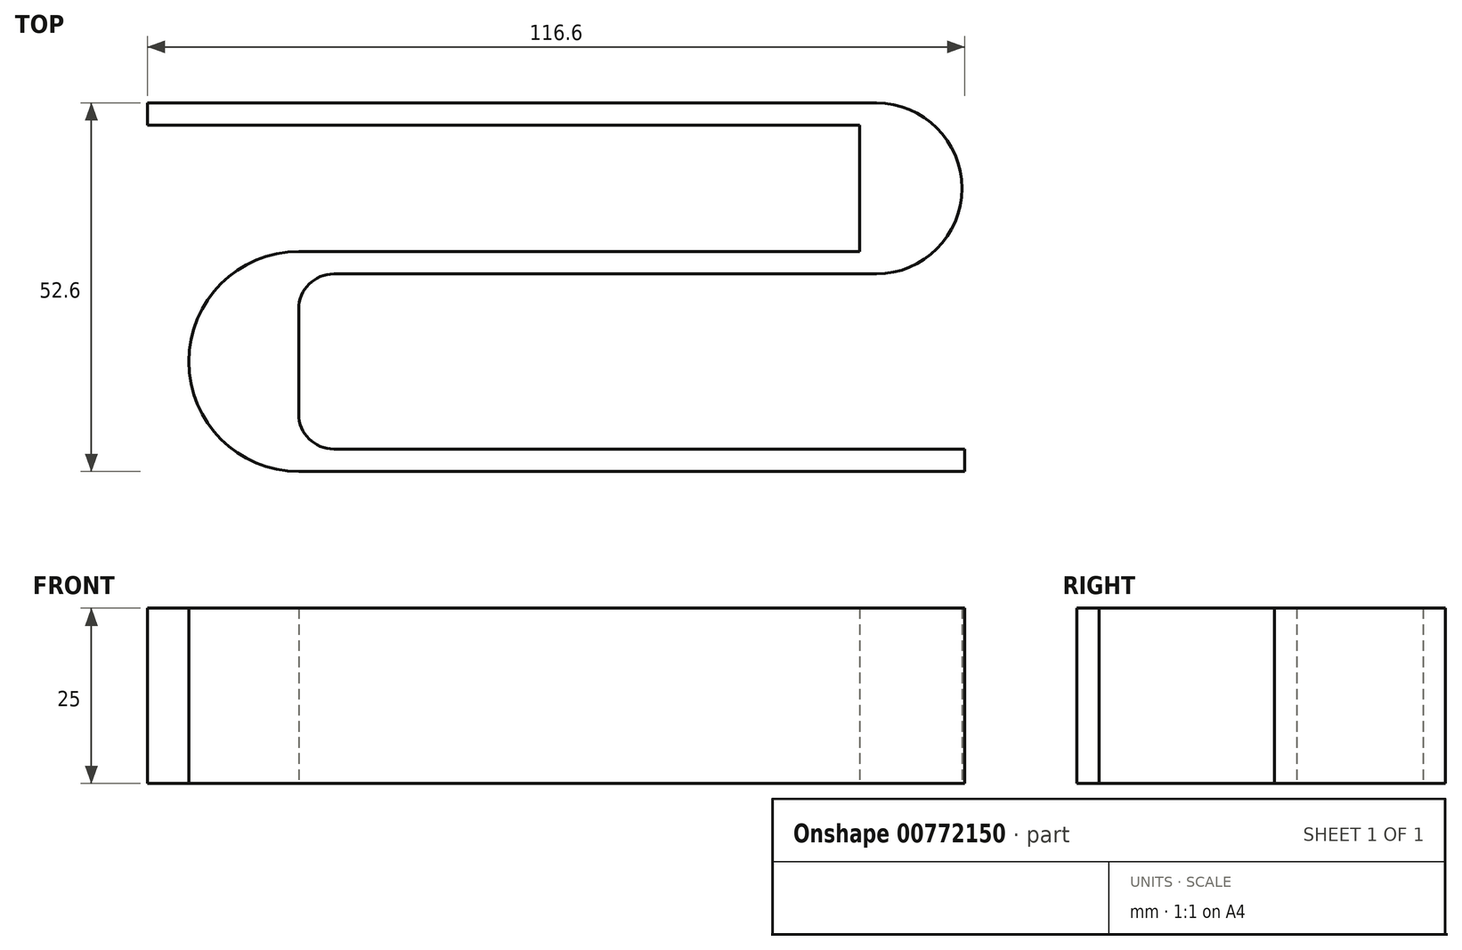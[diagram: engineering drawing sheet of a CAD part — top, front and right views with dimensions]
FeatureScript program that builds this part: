
annotation { "Feature Type Name" : "Feature", "Feature Type Description" : "" }
export const myFeature = defineFeature(function(context is Context, id is Id, definition is map)
    precondition{}
    {
        {
            var Q0;
            Q0=qCreatedBy(makeId("Top.planeOp"),FACE);
            var sketch = newSketch(context, id + "F0", { "sketchPlane" : qUnion([Q0])});
            skLineSegment(sketch, "E0", {"start": v(-21.6, 0) * mm, "end": v(82.4, 0) * mm});
            skLineSegment(sketch, "E1", {"start": v(82.4, 0) * mm, "end": v(82.4, 3.2) * mm});
            skLineSegment(sketch, "E2", {"start": v(82.4, 3.2) * mm, "end": v(-21.6, 3.2) * mm});
            skLineSegment(sketch, "E3", {"start": v(-21.6, 3.2) * mm, "end": v(-21.6, 0) * mm});
            skLineSegment(sketch, "E4", {"start": v(82.4, 0) * mm, "end": v(82.4, -18) * mm});
            skLineSegment(sketch, "E5", {"start": v(82.4, -18) * mm, "end": v(80, -18) * mm});
            skLineSegment(sketch, "E6", {"start": v(80, -18) * mm, "end": v(80, 0) * mm});
            skLineSegment(sketch, "E7", {"start": v(80, -18) * mm, "end": v(0, -18) * mm});
            skLineSegment(sketch, "E8", {"start": v(0, -18) * mm, "end": v(0, -21.2) * mm});
            skLineSegment(sketch, "E9", {"start": v(0, -21.2) * mm, "end": v(82.4, -21.2) * mm});
            skLineSegment(sketch, "E10", {"start": v(82.4, -21.2) * mm, "end": v(82.4, -18) * mm});
            skArc(sketch, "E11", {"start": v(0, -18) * mm, "mid": v(-15.7, -33.7) * mm, "end": v(0, -49.4) * mm});
            skLineSegment(sketch, "E12", {"start": v(0, -21.2) * mm, "end": v(0, -49.4) * mm});
            skArc(sketch, "E13", {"start": v(82.4, -21.2) * mm, "mid": v(94.6, -9) * mm, "end": v(82.4, 3.2) * mm});
            skLineSegment(sketch, "E14", {"start": v(0, -49.4) * mm, "end": v(95, -49.4) * mm});
            skLineSegment(sketch, "E15", {"start": v(0, -46.2) * mm, "end": v(95, -46.2) * mm});
            skLineSegment(sketch, "E16", {"start": v(95, -46.2) * mm, "end": v(95, -49.4) * mm});
            skSolve(sketch);
        }
        {
            var Q0;
            {var subQ0=sQuery(id+"F0.wireOp",EDGE,"E1");Q0=makeQuery(id+"F0.imprint","IMPRINT",FACE,{"disambiguationData":[TD([[makeQuery(id+"F0.imprint","IMPRINT",EDGE,{"derivedFrom":subQ0}),1.0]])]});}
            var Q1;
            {var subQ0=sQuery(id+"F0.wireOp",EDGE,"E4");Q1=makeQuery(id+"F0.imprint","IMPRINT",FACE,{"disambiguationData":[TD([[makeQuery(id+"F0.imprint","IMPRINT",EDGE,{"derivedFrom":subQ0}),-1.0]])]});}
            var Q2;
            Q2=makeQuery(id+"F0.imprint","IMPRINT",FACE,{"disambiguationData":[TD([[makeQuery(id+"F0.imprint","IMPRINT",EDGE,{"derivedFrom":sQuery(id+"F0.wireOp",EDGE,"E1")}),-1.0]])]});
            var Q3;
            Q3=makeQuery(id+"F0.imprint","IMPRINT",FACE,{"disambiguationData":[TD([[makeQuery(id+"F0.imprint","IMPRINT",EDGE,{"derivedFrom":sQuery(id+"F0.wireOp",EDGE,"E5")}),1.0]])]});
            var Q4;
            {var subQ0=sQuery(id+"F0.wireOp",EDGE,"E8");Q4=makeQuery(id+"F0.imprint","IMPRINT",FACE,{"disambiguationData":[TD([[makeQuery(id+"F0.imprint","IMPRINT",EDGE,{"derivedFrom":subQ0}),-1.0]])]});}
            var Q5;
            {var subQ0=sQuery(id+"F0.wireOp",EDGE,"E14");Q5=makeQuery(id+"F0.imprint","IMPRINT",FACE,{"disambiguationData":[TD([[makeQuery(id+"F0.imprint","IMPRINT",EDGE,{"derivedFrom":subQ0}),1.0]])]});}
            var Q6;
            Q6=makeQuery(id+"F0.imprint","IMPRINT",FACE,{"disambiguationData":[TD([[makeQuery(id+"F0.imprint","IMPRINT",EDGE,{"derivedFrom":sQuery(id+"F0.wireOp",EDGE,"E16")}),1.0]])]});
            extrude(context, id + "F1", {"entities" : qUnion([Q0, Q1, Q2, Q3, Q4, Q5, Q6]), "depth" : 25 * mm, "offsetDistance" : 25 * mm});
        }
        {
            var Q0;
            Q0=makeQuery(id+"F1.opExtrude","SWEPT_EDGE",EDGE,{"disambiguationData":[OSD([sQuery(id+"F0.wireOp",EDGE,"E8"),sQuery(id+"F0.wireOp",EDGE,"E9"),sQuery(id+"F0.wireOp",EDGE,"E12")])]});
            var Q1;
            Q1=makeQuery(id+"F1.opExtrude","SWEPT_EDGE",EDGE,{"disambiguationData":[OSD([sQuery(id+"F0.wireOp",EDGE,"E12"),sQuery(id+"F0.wireOp",EDGE,"E15")])]});
            fillet(context, id + "F2", {"entities" : qUnion([Q0, Q1]), "radius" : 5 * mm, "tangentPropagation" : true, "allowEdgeOverflow" : false});
        }
    });
